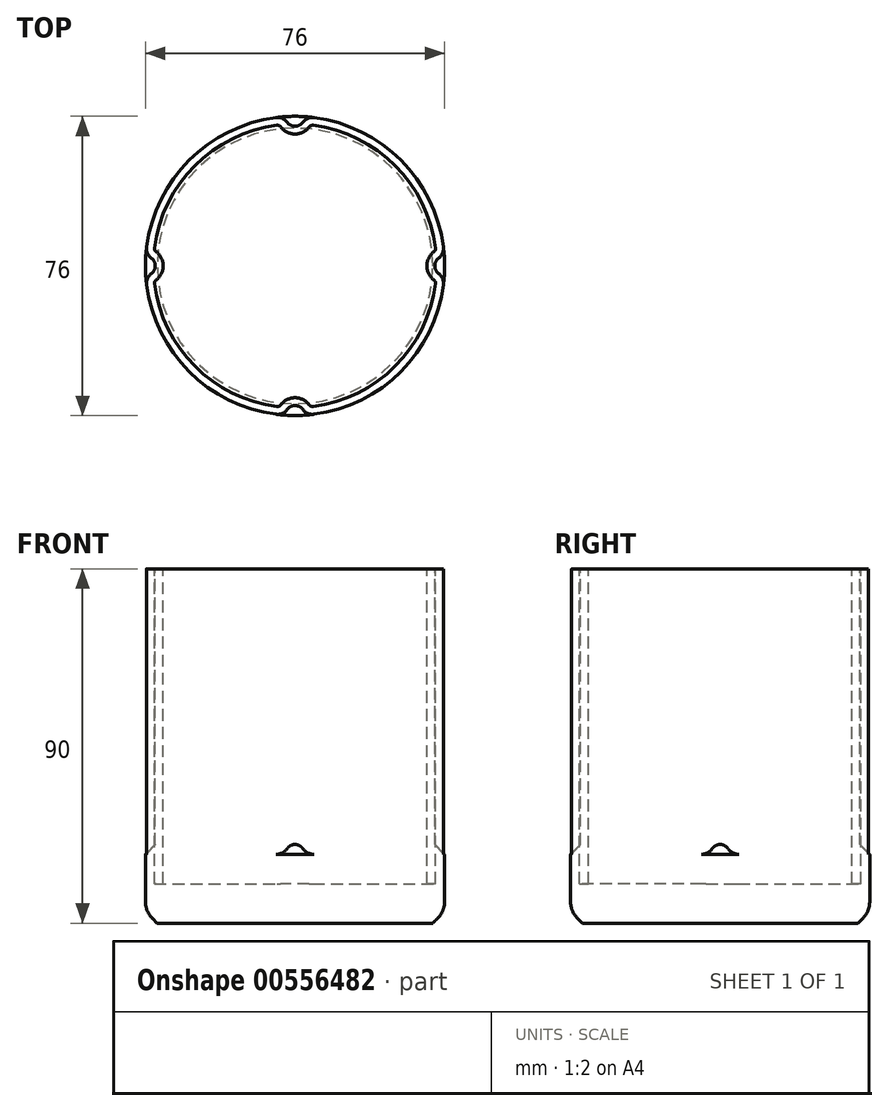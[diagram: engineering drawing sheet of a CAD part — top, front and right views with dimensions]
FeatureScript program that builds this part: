
annotation { "Feature Type Name" : "Feature", "Feature Type Description" : "" }
export const myFeature = defineFeature(function(context is Context, id is Id, definition is map)
    precondition{}
    {
        {
            var Q0;
            Q0=qCreatedBy(makeId("Top.planeOp"),FACE);
            var sketch = newSketch(context, id + "F0", { "sketchPlane" : qUnion([Q0])});
            skCircle(sketch, "E0", {"center": v(0, 0) * mm, "radius": 38 * mm});
            skSolve(sketch);
        }
        {
            var Q0;
            Q0=qSketchRegion(id+"F0",true);
            extrude(context, id + "F1", {"entities" : qUnion([Q0]), "depth" : 90 * mm, "offsetDistance" : 25 * mm});
        }
        {
            var Q0;
            Q0=makeQuery(id+"F1.opExtrude","CAP_EDGE",EDGE,{"disambiguationData":[OSD([sQuery(id+"F0.wireOp",EDGE,"E0")])],"isStart":true});
            chamfer(context, id + "F2", {"entities" : qUnion([Q0]), "width" : 3 * mm, "tangentPropagation" : true});
        }
        {
            var Q0;
            {var subQ0=sQuery(id+"F0.wireOp",EDGE,"E0");Q0=makeQuery(id+"F2.opChamfer","BLEND_EDGE",EDGE,{"blendedFrom":[makeQuery(id+"F1.opExtrude","CAP_EDGE",EDGE,{"disambiguationData":[OSD([subQ0])],"isStart":true}),makeQuery(id+"F1.opExtrude","SWEPT_FACE",FACE,{"disambiguationData":[OSD([subQ0])]})],"blendedInto":[makeQuery(id+"F1.opExtrude","SWEPT_FACE",FACE,{"disambiguationData":[OSD([subQ0])]})]});}
            fillet(context, id + "F3", {"entities" : qUnion([Q0]), "radius" : 6 * mm, "tangentPropagation" : true, "allowEdgeOverflow" : false});
        }
        {
            var Q0;
            Q0=makeQuery(id+"F1.opExtrude","CAP_FACE",FACE,{"disambiguationData":[OSD([sQuery(id+"F0.wireOp",EDGE,"E0")])],"isStart":false});
            var sketch = newSketch(context, id + "F4", { "sketchPlane" : qUnion([Q0])});
            skCircle(sketch, "E1", {"center": v(0, 38) * mm, "radius": 2.5 * mm});
            skCircle(sketch, "E2", {"center": v(-38, 0) * mm, "radius": 2.5 * mm});
            skCircle(sketch, "E3", {"center": v(0, -38) * mm, "radius": 2.5 * mm});
            skCircle(sketch, "E4", {"center": v(38, 0) * mm, "radius": 2.5 * mm});
            skSolve(sketch);
        }
        {
            var Q0;
            Q0 = qSketchRegion(id + "F4", true);
            extrude(context, id + "F5", {"entities" : qUnion([Q0]), "operationType" : NewBodyOperationType.REMOVE, "oppositeDirection" : true, "depth" : 70 * mm, "offsetDistance" : 25 * mm});
        }
        {
            var Q0;
            Q0=makeQuery(id+"F5.boolean.opBoolean","INTERSECT",EDGE,{"disambiguationData":[OD(0.0)],"derivedFrom":[makeQuery(id+"F1.opExtrude","SWEPT_FACE",FACE,{"disambiguationData":[OSD([sQuery(id+"F0.wireOp",EDGE,"E0")])]}),makeQuery(id+"F5.opExtrude","SWEPT_FACE",FACE,{"disambiguationData":[OSD([sQuery(id+"F4.wireOp",EDGE,"E4")])]})]});
            var Q1;
            Q1=makeQuery(id+"F5.boolean.opBoolean","INTERSECT",EDGE,{"disambiguationData":[OD(1.0)],"derivedFrom":[makeQuery(id+"F1.opExtrude","SWEPT_FACE",FACE,{"disambiguationData":[OSD([sQuery(id+"F0.wireOp",EDGE,"E0")])]}),makeQuery(id+"F5.opExtrude","SWEPT_FACE",FACE,{"disambiguationData":[OSD([sQuery(id+"F4.wireOp",EDGE,"E4")])]})]});
            var Q2;
            Q2=makeQuery(id+"F5.boolean.opBoolean","INTERSECT",EDGE,{"disambiguationData":[OD(1.0)],"derivedFrom":[makeQuery(id+"F1.opExtrude","SWEPT_FACE",FACE,{"disambiguationData":[OSD([sQuery(id+"F0.wireOp",EDGE,"E0")])]}),makeQuery(id+"F5.opExtrude","SWEPT_FACE",FACE,{"disambiguationData":[OSD([sQuery(id+"F4.wireOp",EDGE,"E1")])]})]});
            var Q3;
            Q3=makeQuery(id+"F5.boolean.opBoolean","INTERSECT",EDGE,{"disambiguationData":[OD(0.0)],"derivedFrom":[makeQuery(id+"F1.opExtrude","SWEPT_FACE",FACE,{"disambiguationData":[OSD([sQuery(id+"F0.wireOp",EDGE,"E0")])]}),makeQuery(id+"F5.opExtrude","SWEPT_FACE",FACE,{"disambiguationData":[OSD([sQuery(id+"F4.wireOp",EDGE,"E1")])]})]});
            var Q4;
            Q4=makeQuery(id+"F5.boolean.opBoolean","INTERSECT",EDGE,{"disambiguationData":[OD(1.0)],"derivedFrom":[makeQuery(id+"F1.opExtrude","SWEPT_FACE",FACE,{"disambiguationData":[OSD([sQuery(id+"F0.wireOp",EDGE,"E0")])]}),makeQuery(id+"F5.opExtrude","SWEPT_FACE",FACE,{"disambiguationData":[OSD([sQuery(id+"F4.wireOp",EDGE,"E2")])]})]});
            var Q5;
            Q5=makeQuery(id+"F5.boolean.opBoolean","INTERSECT",EDGE,{"disambiguationData":[OD(0.0)],"derivedFrom":[makeQuery(id+"F1.opExtrude","SWEPT_FACE",FACE,{"disambiguationData":[OSD([sQuery(id+"F0.wireOp",EDGE,"E0")])]}),makeQuery(id+"F5.opExtrude","SWEPT_FACE",FACE,{"disambiguationData":[OSD([sQuery(id+"F4.wireOp",EDGE,"E2")])]})]});
            var Q6;
            Q6=makeQuery(id+"F5.boolean.opBoolean","INTERSECT",EDGE,{"disambiguationData":[OD(1.0)],"derivedFrom":[makeQuery(id+"F1.opExtrude","SWEPT_FACE",FACE,{"disambiguationData":[OSD([sQuery(id+"F0.wireOp",EDGE,"E0")])]}),makeQuery(id+"F5.opExtrude","SWEPT_FACE",FACE,{"disambiguationData":[OSD([sQuery(id+"F4.wireOp",EDGE,"E3")])]})]});
            var Q7;
            Q7=makeQuery(id+"F5.boolean.opBoolean","INTERSECT",EDGE,{"disambiguationData":[OD(0.0)],"derivedFrom":[makeQuery(id+"F1.opExtrude","SWEPT_FACE",FACE,{"disambiguationData":[OSD([sQuery(id+"F0.wireOp",EDGE,"E0")])]}),makeQuery(id+"F5.opExtrude","SWEPT_FACE",FACE,{"disambiguationData":[OSD([sQuery(id+"F4.wireOp",EDGE,"E3")])]})]});
            fillet(context, id + "F6", {"entities" : qUnion([Q0, Q1, Q2, Q3, Q4, Q5, Q6, Q7]), "radius" : 3 * mm, "tangentPropagation" : true, "allowEdgeOverflow" : false});
        }
        {
            var Q0;
            Q0=makeQuery(id+"F5.boolean.opBoolean","INTERSECT",EDGE,{"derivedFrom":[makeQuery(id+"F1.opExtrude","SWEPT_FACE",FACE,{"disambiguationData":[OSD([sQuery(id+"F0.wireOp",EDGE,"E0")])]}),makeQuery(id+"F5.opExtrude","CAP_FACE",FACE,{"disambiguationData":[OSD([sQuery(id+"F4.wireOp",EDGE,"E3")])],"isStart":false})]});
            var Q1;
            Q1=makeQuery(id+"F5.boolean.opBoolean","INTERSECT",EDGE,{"derivedFrom":[makeQuery(id+"F1.opExtrude","SWEPT_FACE",FACE,{"disambiguationData":[OSD([sQuery(id+"F0.wireOp",EDGE,"E0")])]}),makeQuery(id+"F5.opExtrude","CAP_FACE",FACE,{"disambiguationData":[OSD([sQuery(id+"F4.wireOp",EDGE,"E4")])],"isStart":false})]});
            var Q2;
            Q2=makeQuery(id+"F5.boolean.opBoolean","INTERSECT",EDGE,{"derivedFrom":[makeQuery(id+"F1.opExtrude","SWEPT_FACE",FACE,{"disambiguationData":[OSD([sQuery(id+"F0.wireOp",EDGE,"E0")])]}),makeQuery(id+"F5.opExtrude","CAP_FACE",FACE,{"disambiguationData":[OSD([sQuery(id+"F4.wireOp",EDGE,"E1")])],"isStart":false})]});
            var Q3;
            Q3=makeQuery(id+"F5.boolean.opBoolean","INTERSECT",EDGE,{"derivedFrom":[makeQuery(id+"F1.opExtrude","SWEPT_FACE",FACE,{"disambiguationData":[OSD([sQuery(id+"F0.wireOp",EDGE,"E0")])]}),makeQuery(id+"F5.opExtrude","CAP_FACE",FACE,{"disambiguationData":[OSD([sQuery(id+"F4.wireOp",EDGE,"E2")])],"isStart":false})]});
            chamfer(context, id + "F7", {"entities" : qUnion([Q0, Q1, Q2, Q3]), "width" : 2.5 * mm, "tangentPropagation" : true});
        }
        {
            var Q0;
            Q0=qCreatedBy(makeId("Top.planeOp"),FACE);
            cPlane(context, id + "F8", {"entities" : qUnion([Q0]), "cplaneType" : CPlaneType.OFFSET, "offset" : 100 * mm, "width" : 150 * mm, "height" : 150 * mm});
        }
        {
            var Q0;
            Q0=qCreatedBy(id+"F8.planeOp",FACE);
            var sketch = newSketch(context, id + "F9", { "sketchPlane" : qUnion([Q0])});
            skArc(sketch, "E5.0", {"start": v(-3.61, 35.32) * mm, "mid": v(-4.02, 35.64) * mm, "end": v(-4.54, 35.71) * mm});
            skArc(sketch, "E5.1", {"start": v(3.61, 35.32) * mm, "mid": v(0, 33.5) * mm, "end": v(-3.61, 35.32) * mm});
            skArc(sketch, "E5.2", {"start": v(4.54, 35.71) * mm, "mid": v(4.02, 35.64) * mm, "end": v(3.61, 35.32) * mm});
            skArc(sketch, "E5.3", {"start": v(35.71, 4.54) * mm, "mid": v(25.46, 25.46) * mm, "end": v(4.54, 35.71) * mm});
            skArc(sketch, "E5.4", {"start": v(35.32, 3.61) * mm, "mid": v(35.64, 4.02) * mm, "end": v(35.71, 4.54) * mm});
            skArc(sketch, "E5.5", {"start": v(-35.71, -4.54) * mm, "mid": v(-25.46, -25.46) * mm, "end": v(-4.54, -35.71) * mm});
            skArc(sketch, "E5.6", {"start": v(-35.32, -3.61) * mm, "mid": v(-35.64, -4.02) * mm, "end": v(-35.71, -4.54) * mm});
            skArc(sketch, "E5.7", {"start": v(-35.32, 3.61) * mm, "mid": v(-33.5, 0) * mm, "end": v(-35.32, -3.61) * mm});
            skArc(sketch, "E5.8", {"start": v(-35.71, 4.54) * mm, "mid": v(-35.64, 4.02) * mm, "end": v(-35.32, 3.61) * mm});
            skArc(sketch, "E5.9", {"start": v(-4.54, -35.71) * mm, "mid": v(-4.02, -35.64) * mm, "end": v(-3.61, -35.32) * mm});
            skArc(sketch, "E5.10", {"start": v(-3.61, -35.32) * mm, "mid": v(0, -33.5) * mm, "end": v(3.61, -35.32) * mm});
            skArc(sketch, "E5.11", {"start": v(3.61, -35.32) * mm, "mid": v(4.02, -35.64) * mm, "end": v(4.54, -35.71) * mm});
            skArc(sketch, "E5.12", {"start": v(4.54, -35.71) * mm, "mid": v(25.46, -25.46) * mm, "end": v(35.71, -4.54) * mm});
            skArc(sketch, "E5.13", {"start": v(35.71, -4.54) * mm, "mid": v(35.64, -4.02) * mm, "end": v(35.32, -3.61) * mm});
            skArc(sketch, "E5.14", {"start": v(-4.54, 35.71) * mm, "mid": v(-25.46, 25.46) * mm, "end": v(-35.71, 4.54) * mm});
            skArc(sketch, "E5.15", {"start": v(35.32, -3.61) * mm, "mid": v(33.5, 0) * mm, "end": v(35.32, 3.61) * mm});
            skSolve(sketch);
        }
        {
            var Q0;
            Q0=makeQuery(id+"F9.imprint","IMPRINT",FACE,{"disambiguationData":[TD([[makeQuery(id+"F9.imprint","IMPRINT",EDGE,{"derivedFrom":sQuery(id+"F9.wireOp",EDGE,"E5.0")}),1.0]])]});
            extrude(context, id + "F10", {"entities" : qUnion([Q0]), "operationType" : NewBodyOperationType.REMOVE, "oppositeDirection" : true, "depth" : 90 * mm, "offsetDistance" : 25 * mm});
        }
    });
